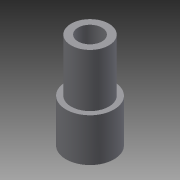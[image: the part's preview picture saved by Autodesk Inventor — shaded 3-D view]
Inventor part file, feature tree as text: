
AUTODESK INVENTOR PART (.ipt)
format: ipt  version: 2013 (Build 170138000, 138)  size: 102,400 bytes
history: native  units: in
note: dims shown in document units (in); Inventor stores cm internally (conversion verified against a paired STEP export)
features: sketch x3, extrude x2, hole x1
ambient origin geometry x8: Origin, YZ Plane, XZ Plane, XY Plane, X Axis, Y Axis, Z Axis, Center Point
bodies: Solid1 (feature_tree)
feature tree (6):
  extrude  "Extrusion1"  Depth=0.25in
  extrude  "Extrusion2"  Depth=0.3937in
  hole  "Hole1"  [1 undecoded]
  sketch  "Sketch1"  dims[d0=0.5in d1=0.25in]
  sketch  "Sketch2"  dims[d2=1.0in d3=0.0in d4=0.3937in]
  sketch  "Sketch3"  dims[d5=0.5512in d6=0.0in d7=0.2in d8=0.6in d9=0.085in d10=0.75in d11=0.375in d12=0.25in d13=0.5635in d14=1.0in d15=0.8108in]
note: 1 required parameter value undecoded (feature->parameter linkage not recoverable at this tier; creation-order binding heuristic only, values carry confidence <= 0.55)
